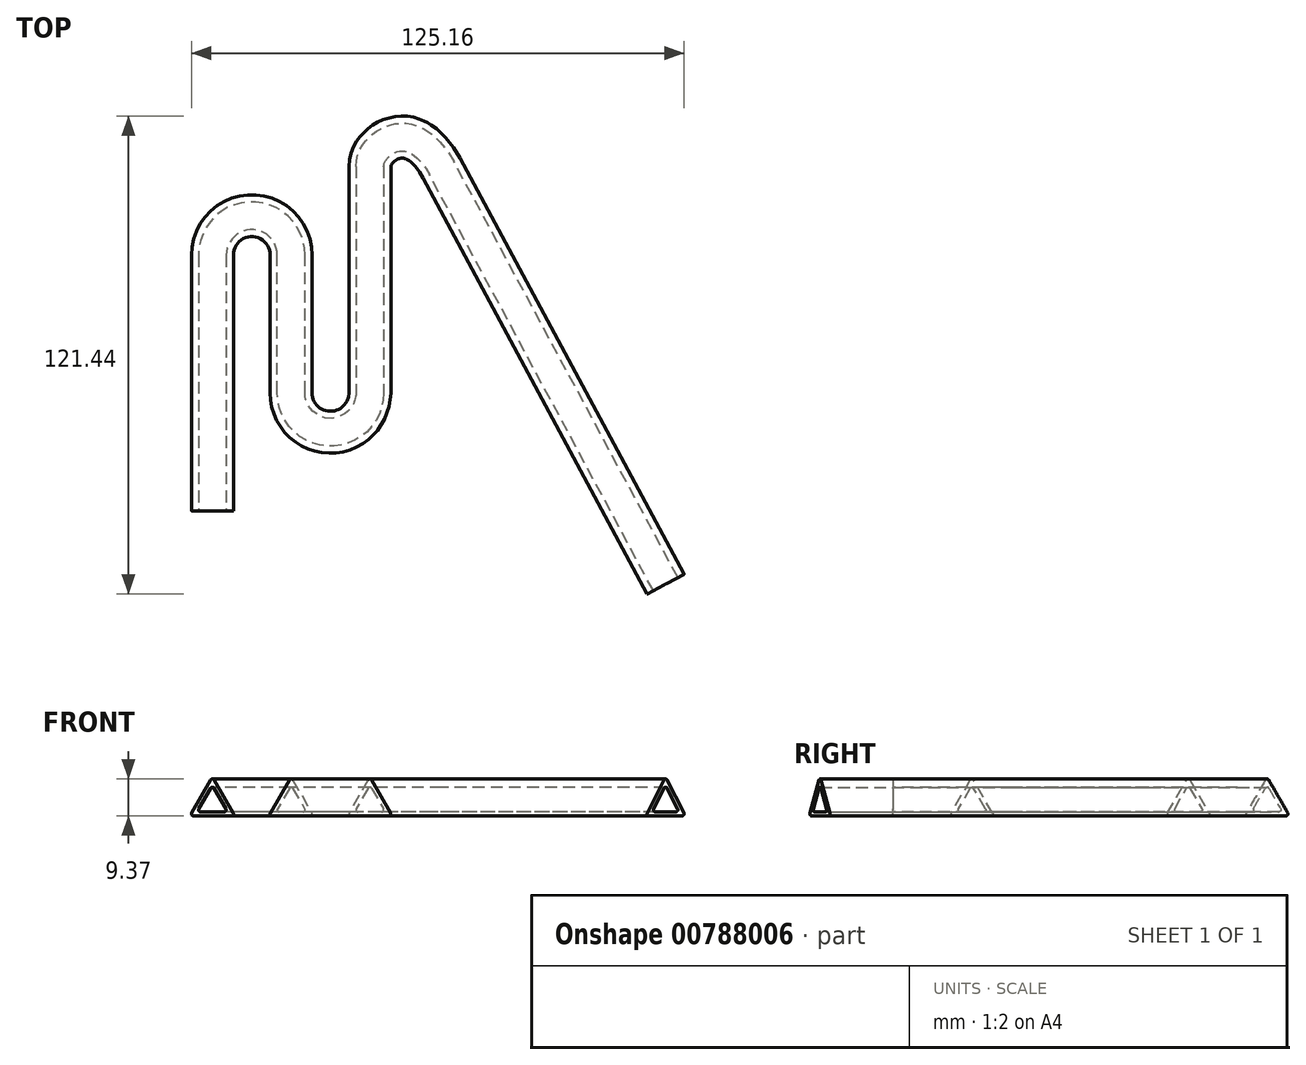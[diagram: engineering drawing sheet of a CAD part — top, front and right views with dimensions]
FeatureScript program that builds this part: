
annotation { "Feature Type Name" : "Feature", "Feature Type Description" : "" }
export const myFeature = defineFeature(function(context is Context, id is Id, definition is map)
    precondition{}
    {
        {
            var Q0;
            Q0=qCreatedBy(makeId("Top.planeOp"),FACE);
            var sketch = newSketch(context, id + "F0", { "sketchPlane" : qUnion([Q0])});
            skLineSegment(sketch, "E0", {"start": v(-40, -24.53) * mm, "end": v(-40, 40.47) * mm});
            skArc(sketch, "E1", {"start": v(-20, 40.47) * mm, "mid": v(-30, 50.47) * mm, "end": v(-40, 40.47) * mm});
            skLineSegment(sketch, "E2", {"start": v(-20, 40.47) * mm, "end": v(-20, 5.47) * mm});
            skArc(sketch, "E3", {"start": v(-20, 5.47) * mm, "mid": v(-10, -4.53) * mm, "end": v(0, 5.47) * mm});
            skLineSegment(sketch, "E4", {"start": v(0, 5.47) * mm, "end": v(0, 62.97) * mm});
            skLineSegment(sketch, "E5", {"start": v(18.26, 62.55) * mm, "end": v(75.14, -43.11) * mm});
            skFitSpline(sketch, "E6", {"points": [v(0, 62.97) * mm, v(8.1, 70.47) * mm, v(18.26, 62.55) * mm], "startDerivative": vector(0, 25.2) * mm, "endDerivative": vector(13.1, -24.55) * mm});
            skLineSegment(sketch, "E7", {"start": v(-30, 50.47) * mm, "end": v(-50.03, 50.47) * mm, "construction": true});
            skLineSegment(sketch, "E8", {"start": v(-10, -4.53) * mm, "end": v(16.8, -4.53) * mm, "construction": true});
            skLineSegment(sketch, "E9", {"start": v(8.1, 70.47) * mm, "end": v(-14.96, 70.47) * mm, "construction": true});
            skLineSegment(sketch, "E10", {"start": v(-40, -24.53) * mm, "end": v(19.35, -24.53) * mm, "construction": true});
            skSolve(sketch);
        }
        {
            var Q0;
            Q0=qCreatedBy(makeId("Front.planeOp"),FACE);
            var sketch = newSketch(context, id + "F1", { "sketchPlane" : qUnion([Q0])});
            skPoint(sketch, "E11.0", {"position": v(-40, 0) * mm});
            skLineSegment(sketch, "E12", {"start": v(-40, 0) * mm, "end": v(-43.9, -2.25) * mm, "construction": true});
            skLineSegment(sketch, "E13", {"start": v(-40, 0) * mm, "end": v(-40, 4.5) * mm, "construction": true});
            skLineSegment(sketch, "E14", {"start": v(-40, 0) * mm, "end": v(-36.1, -2.25) * mm, "construction": true});
            skLineSegment(sketch, "E15", {"start": v(-40.43, 3.75) * mm, "end": v(-43.46, -1.5) * mm});
            skLineSegment(sketch, "E16", {"start": v(-43.03, -2.25) * mm, "end": v(-36.97, -2.25) * mm});
            skLineSegment(sketch, "E17", {"start": v(-39.57, 3.75) * mm, "end": v(-36.54, -1.5) * mm});
            skLineSegment(sketch, "E18.0", {"start": v(-40.43, 5.83) * mm, "end": v(-45.26, -2.54) * mm});
            skLineSegment(sketch, "E18.1", {"start": v(-39.57, 5.83) * mm, "end": v(-34.74, -2.54) * mm});
            skLineSegment(sketch, "E18.2", {"start": v(-44.83, -3.29) * mm, "end": v(-35.17, -3.29) * mm});
            skPoint(sketch, "E19.visualSharp", {"position": v(-40, 6.58) * mm});
            skArc(sketch, "E19.filletArc", {"start": v(-39.57, 5.83) * mm, "mid": v(-40, 6.08) * mm, "end": v(-40.43, 5.83) * mm});
            skPoint(sketch, "E20.visualSharp", {"position": v(-40, 4.5) * mm});
            skArc(sketch, "E20.filletArc", {"start": v(-39.57, 3.75) * mm, "mid": v(-40, 4) * mm, "end": v(-40.43, 3.75) * mm});
            skPoint(sketch, "E21.visualSharp", {"position": v(-45.7, -3.29) * mm});
            skArc(sketch, "E21.filletArc", {"start": v(-45.26, -2.54) * mm, "mid": v(-45.26, -3.04) * mm, "end": v(-44.83, -3.29) * mm});
            skPoint(sketch, "E22.visualSharp", {"position": v(-43.9, -2.25) * mm});
            skArc(sketch, "E22.filletArc", {"start": v(-43.46, -1.5) * mm, "mid": v(-43.46, -2) * mm, "end": v(-43.03, -2.25) * mm});
            skPoint(sketch, "E23.visualSharp", {"position": v(-36.1, -2.25) * mm});
            skArc(sketch, "E23.filletArc", {"start": v(-36.97, -2.25) * mm, "mid": v(-36.54, -2) * mm, "end": v(-36.54, -1.5) * mm});
            skPoint(sketch, "E24.visualSharp", {"position": v(-34.3, -3.29) * mm});
            skArc(sketch, "E24.filletArc", {"start": v(-35.17, -3.29) * mm, "mid": v(-34.74, -3.04) * mm, "end": v(-34.74, -2.54) * mm});
            skPoint(sketch, "E25", {"position": v(-42.44, 0.27) * mm});
            skLineSegment(sketch, "E26", {"start": v(-42.44, 0.27) * mm, "end": v(-43.64, 0.27) * mm, "construction": true});
            skSolve(sketch);
        }
        {
            var Q0;
            Q0=makeQuery(id+"F1.imprint","IMPRINT",FACE,{"disambiguationData":[TD([[makeQuery(id+"F1.imprint","IMPRINT",EDGE,{"derivedFrom":sQuery(id+"F1.wireOp",EDGE,"E15")}),-1.0]])]});
            var Q1;
            Q1=sQuery(id+"F0.wireOp",EDGE,"E0");
            var Q2;
            Q2=sQuery(id+"F0.wireOp",EDGE,"E1");
            var Q3;
            Q3=sQuery(id+"F0.wireOp",EDGE,"E2");
            var Q4;
            Q4=sQuery(id+"F0.wireOp",EDGE,"E3");
            var Q5;
            Q5=sQuery(id+"F0.wireOp",EDGE,"E4");
            var Q6;
            Q6=sQuery(id+"F0.wireOp",EDGE,"E6");
            var Q7;
            Q7=sQuery(id+"F0.wireOp",EDGE,"E5");
            sweep(context, id + "F2", {"profiles" : qUnion([Q0]), "path" : qUnion([Q1, Q2, Q3, Q4, Q5, Q6, Q7])});
        }
    });
